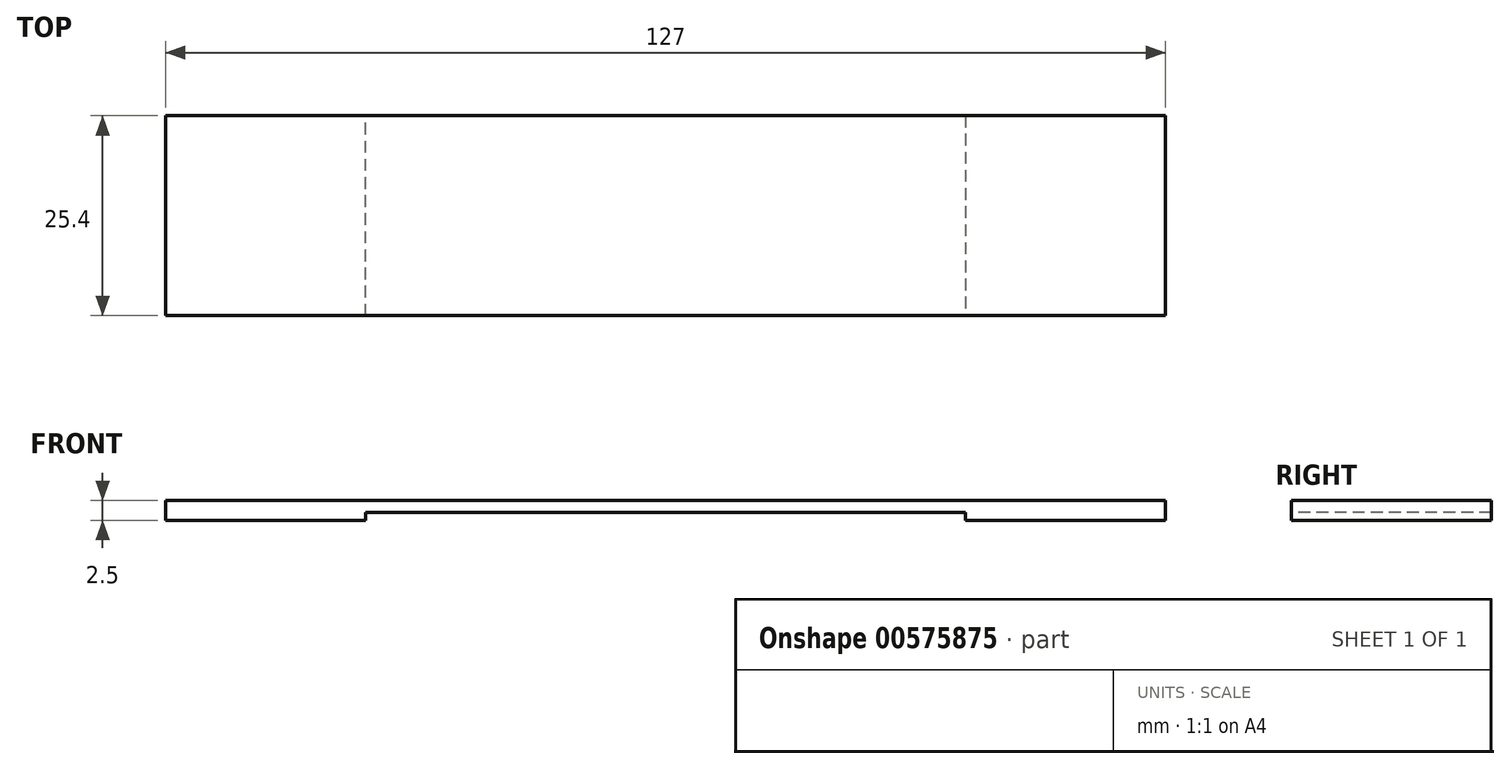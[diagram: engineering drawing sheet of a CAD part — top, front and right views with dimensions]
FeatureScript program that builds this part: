
annotation { "Feature Type Name" : "Feature", "Feature Type Description" : "" }
export const myFeature = defineFeature(function(context is Context, id is Id, definition is map)
    precondition{}
    {
        {
            var Q0;
            Q0=qCreatedBy(makeId("Top.planeOp"),FACE);
            var sketch = newSketch(context, id + "F0", { "sketchPlane" : qUnion([Q0])});
            skLineSegment(sketch, "E0.bottom", {"start": v(0, 0) * mm, "end": v(127, 0) * mm});
            skLineSegment(sketch, "E0.top", {"start": v(0, 25.4) * mm, "end": v(127, 25.4) * mm});
            skLineSegment(sketch, "E0.left", {"start": v(0, 0) * mm, "end": v(0, 25.4) * mm});
            skLineSegment(sketch, "E0.right", {"start": v(127, 0) * mm, "end": v(127, 25.4) * mm});
            skSolve(sketch);
        }
        {
            var Q0;
            Q0 = qSketchRegion(id + "F0", true);
            extrude(context, id + "F1", {"entities" : qUnion([Q0]), "depth" : 1.5 * mm, "offsetDistance" : 25 * mm});
        }
        {
            var Q0;
            Q0=makeQuery(id+"F1.opExtrude","CAP_FACE",FACE,{"disambiguationData":[OSD([sQuery(id+"F0.wireOp",EDGE,"E0.bottom"),sQuery(id+"F0.wireOp",EDGE,"E0.top"),sQuery(id+"F0.wireOp",EDGE,"E0.left"),sQuery(id+"F0.wireOp",EDGE,"E0.right")])],"isStart":true});
            var sketch = newSketch(context, id + "F2", { "sketchPlane" : qUnion([Q0])});
            skLineSegment(sketch, "E1.bottom", {"start": v(0, 0) * mm, "end": v(25.4, 0) * mm});
            skLineSegment(sketch, "E1.top", {"start": v(0, -25.4) * mm, "end": v(25.4, -25.4) * mm});
            skLineSegment(sketch, "E1.left", {"start": v(0, 0) * mm, "end": v(0, -25.4) * mm});
            skLineSegment(sketch, "E1.right", {"start": v(25.4, 0) * mm, "end": v(25.4, -25.4) * mm});
            skSolve(sketch);
        }
        {
            var Q0;
            Q0 = qSketchRegion(id + "F2", true);
            extrude(context, id + "F3", {"entities" : qUnion([Q0]), "operationType" : NewBodyOperationType.ADD, "depth" : 1 * mm, "offsetDistance" : 25 * mm});
        }
        {
            var Q0;
            Q0=makeQuery(id+"F1.opExtrude","CAP_FACE",FACE,{"disambiguationData":[OSD([sQuery(id+"F0.wireOp",EDGE,"E0.bottom"),sQuery(id+"F0.wireOp",EDGE,"E0.top"),sQuery(id+"F0.wireOp",EDGE,"E0.left"),sQuery(id+"F0.wireOp",EDGE,"E0.right")])],"isStart":true});
            var sketch = newSketch(context, id + "F4", { "sketchPlane" : qUnion([Q0])});
            skLineSegment(sketch, "E2.bottom", {"start": v(127, -25.4) * mm, "end": v(101.6, -25.4) * mm});
            skLineSegment(sketch, "E2.top", {"start": v(127, 0) * mm, "end": v(101.6, 0) * mm});
            skLineSegment(sketch, "E2.left", {"start": v(127, -25.4) * mm, "end": v(127, 0) * mm});
            skLineSegment(sketch, "E2.right", {"start": v(101.6, -25.4) * mm, "end": v(101.6, 0) * mm});
            skSolve(sketch);
        }
        {
            var Q0;
            Q0 = qSketchRegion(id + "F4", true);
            extrude(context, id + "F5", {"entities" : qUnion([Q0]), "operationType" : NewBodyOperationType.ADD, "depth" : 1 * mm, "offsetDistance" : 25 * mm});
        }
    });
